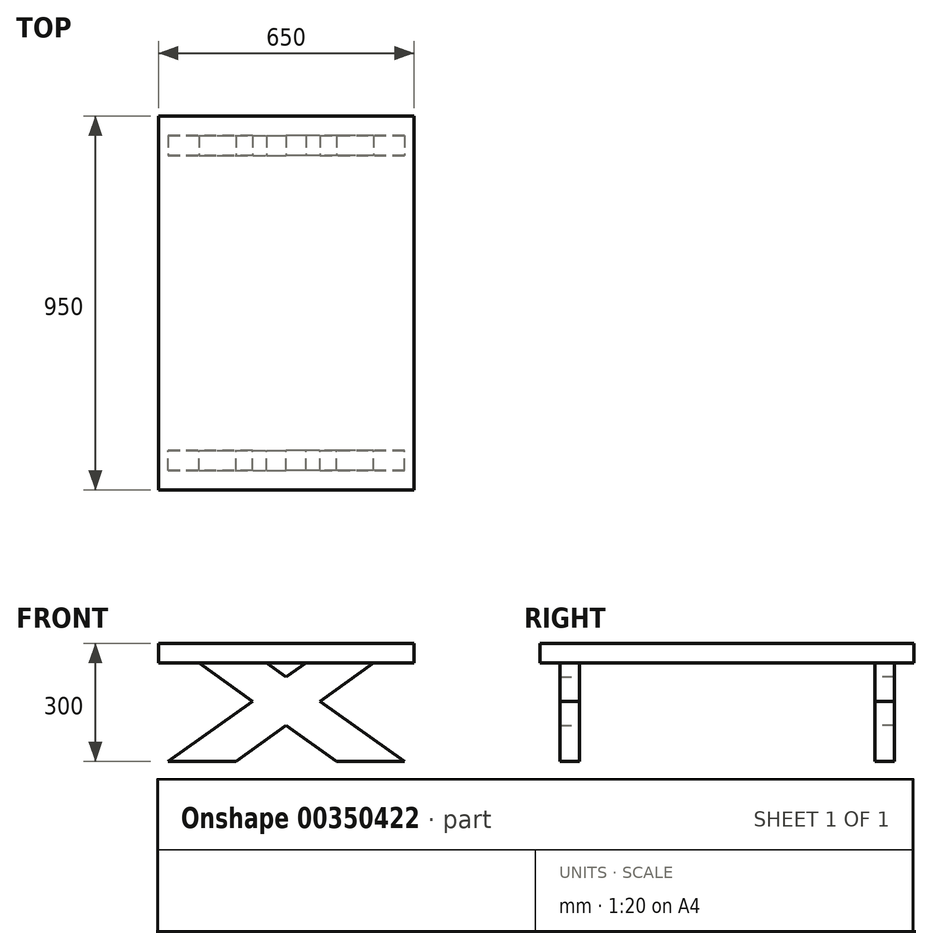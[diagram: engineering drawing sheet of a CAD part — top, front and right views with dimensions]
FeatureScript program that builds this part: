
annotation { "Feature Type Name" : "Feature", "Feature Type Description" : "" }
export const myFeature = defineFeature(function(context is Context, id is Id, definition is map)
    precondition{}
    {
        {
            var Q0;
            Q0=qCreatedBy(makeId("Top.planeOp"),FACE);
            var sketch = newSketch(context, id + "F0", { "sketchPlane" : qUnion([Q0])});
            skLineSegment(sketch, "E0.bottom", {"start": v(325, -475) * mm, "end": v(-325, -475) * mm});
            skLineSegment(sketch, "E0.top", {"start": v(325, 475) * mm, "end": v(-325, 475) * mm});
            skLineSegment(sketch, "E0.left", {"start": v(325, -475) * mm, "end": v(325, 475) * mm});
            skLineSegment(sketch, "E0.right", {"start": v(-325, -475) * mm, "end": v(-325, 475) * mm});
            skPoint(sketch, "E0.middle", {"position": v(0, 0) * mm});
            skSolve(sketch);
        }
        {
            var Q0;
            Q0=makeQuery(id+"F0.imprint","IMPRINT",FACE,{"disambiguationData":[TD([[makeQuery(id+"F0.imprint","IMPRINT",EDGE,{"derivedFrom":sQuery(id+"F0.wireOp",EDGE,"E0.bottom")}),-1.0]])]});
            extrude(context, id + "F1", {"entities" : qUnion([Q0]), "depth" : 50 * mm});
        }
        {
            var Q0;
            Q0=makeQuery(id+"F1.opExtrude","SWEPT_FACE",FACE,{"disambiguationData":[OSD([sQuery(id+"F0.wireOp",EDGE,"E0.bottom")])]});
            cPlane(context, id + "F2", {"entities" : qUnion([Q0]), "cplaneType" : CPlaneType.OFFSET, "offset" : 100 * mm, "oppositeDirection" : true, "width" : 150 * mm, "height" : 150 * mm});
        }
        {
            var Q0;
            Q0=qCreatedBy(id+"F2.planeOp",FACE);
            var sketch = newSketch(context, id + "F3", { "sketchPlane" : qUnion([Q0])});
            skLineSegment(sketch, "E1", {"start": v(0, 0) * mm, "end": v(0, -250) * mm, "construction": true});
            skLineSegment(sketch, "E2", {"start": v(-222.05, 0) * mm, "end": v(-50, 0) * mm});
            skLineSegment(sketch, "E3", {"start": v(-50, 0) * mm, "end": v(300, -250) * mm});
            skLineSegment(sketch, "E4", {"start": v(300, -250) * mm, "end": v(127.95, -250) * mm});
            skLineSegment(sketch, "E5", {"start": v(127.95, -250) * mm, "end": v(-222.05, 0) * mm});
            skLineSegment(sketch, "E6.MirrorCS", {"start": v(50, 0) * mm, "end": v(-300, -250) * mm});
            skLineSegment(sketch, "E7.MirrorCS", {"start": v(222.05, 0) * mm, "end": v(50, 0) * mm});
            skLineSegment(sketch, "E8.MirrorCS", {"start": v(-127.95, -250) * mm, "end": v(222.05, 0) * mm});
            skLineSegment(sketch, "E9.MirrorCS", {"start": v(-300, -250) * mm, "end": v(-127.95, -250) * mm});
            skSolve(sketch);
        }
        {
            var Q0;
            {var subQ5=sQuery(id+"F3.wireOp",EDGE,"E9.MirrorCS");Q0=makeQuery(id+"F3.imprint","IMPRINT",FACE,{"disambiguationData":[TD([[makeQuery(id+"F3.imprint","IMPRINT",EDGE,{"derivedFrom":subQ5}),1.0]])]});}
            var Q1;
            {var subQ0=sQuery(id+"F3.wireOp",EDGE,"E6.MirrorCS");var subQ1=sQuery(id+"F3.wireOp",EDGE,"E3");var subQ2=makeQuery(id+"F3.imprint","INTERSECT",VERTEX,{"derivedFrom":[subQ1,subQ0]});Q1=makeQuery(id+"F3.imprint","IMPRINT",FACE,{"disambiguationData":[TD([[makeQuery(id+"F3.imprint","IMPRINT",EDGE,{"disambiguationData":[TD([[subQ2,-1.0]])],"derivedFrom":subQ1}),-1.0]])]});}
            var Q2;
            {var subQ5=sQuery(id+"F3.wireOp",EDGE,"E7.MirrorCS");Q2=makeQuery(id+"F3.imprint","IMPRINT",FACE,{"disambiguationData":[TD([[makeQuery(id+"F3.imprint","IMPRINT",EDGE,{"derivedFrom":subQ5}),1.0]])]});}
            var Q3;
            {var subQ0=sQuery(id+"F3.wireOp",EDGE,"E2");Q3=makeQuery(id+"F3.imprint","IMPRINT",FACE,{"disambiguationData":[TD([[makeQuery(id+"F3.imprint","IMPRINT",EDGE,{"derivedFrom":subQ0}),-1.0]])]});}
            var Q4;
            {var subQ0=sQuery(id+"F3.wireOp",EDGE,"E4");Q4=makeQuery(id+"F3.imprint","IMPRINT",FACE,{"disambiguationData":[TD([[makeQuery(id+"F3.imprint","IMPRINT",EDGE,{"derivedFrom":subQ0}),-1.0]])]});}
            var Q5;
            {var subQ5=sQuery(id+"F3.wireOp",EDGE,"E9.MirrorCS");Q5=makeQuery(id+"F3.imprint","IMPRINT",FACE,{"disambiguationData":[TD([[makeQuery(id+"F3.imprint","IMPRINT",EDGE,{"derivedFrom":subQ5}),1.0]])]});}
            var Q6;
            {var subQ0=sQuery(id+"F3.wireOp",EDGE,"E2");Q6=makeQuery(id+"F3.imprint","IMPRINT",FACE,{"disambiguationData":[TD([[makeQuery(id+"F3.imprint","IMPRINT",EDGE,{"derivedFrom":subQ0}),-1.0]])]});}
            var Q7;
            {var subQ0=sQuery(id+"F3.wireOp",EDGE,"E6.MirrorCS");var subQ1=sQuery(id+"F3.wireOp",EDGE,"E3");var subQ2=makeQuery(id+"F3.imprint","INTERSECT",VERTEX,{"derivedFrom":[subQ1,subQ0]});Q7=makeQuery(id+"F3.imprint","IMPRINT",FACE,{"disambiguationData":[TD([[makeQuery(id+"F3.imprint","IMPRINT",EDGE,{"disambiguationData":[TD([[subQ2,-1.0]])],"derivedFrom":subQ1}),-1.0]])]});}
            var Q8;
            {var subQ5=sQuery(id+"F3.wireOp",EDGE,"E7.MirrorCS");Q8=makeQuery(id+"F3.imprint","IMPRINT",FACE,{"disambiguationData":[TD([[makeQuery(id+"F3.imprint","IMPRINT",EDGE,{"derivedFrom":subQ5}),1.0]])]});}
            var Q9;
            {var subQ0=sQuery(id+"F3.wireOp",EDGE,"E4");Q9=makeQuery(id+"F3.imprint","IMPRINT",FACE,{"disambiguationData":[TD([[makeQuery(id+"F3.imprint","IMPRINT",EDGE,{"derivedFrom":subQ0}),-1.0]])]});}
            extrude(context, id + "F4", {"entities" : qUnion([Q0, Q1, Q2, Q3, Q4, Q5, Q6, Q7, Q8, Q9]), "operationType" : NewBodyOperationType.ADD, "depth" : 50 * mm});
        }
        {
            var Q0;
            Q0=makeQuery(id+"F1.opExtrude","SWEPT_BODY",BODY,{"disambiguationData":[OSD([sQuery(id+"F0.wireOp",EDGE,"E0.bottom"),sQuery(id+"F0.wireOp",EDGE,"E0.top"),sQuery(id+"F0.wireOp",EDGE,"E0.left"),sQuery(id+"F0.wireOp",EDGE,"E0.right")])]});
            var Q1;
            Q1=qCreatedBy(makeId("Front.planeOp"),FACE);
            mirror(context, id + "F5", {"operationType" : NewBodyOperationType.ADD, "entities" : qUnion([Q0]), "mirrorPlane" : qUnion([Q1])});
        }
    });
